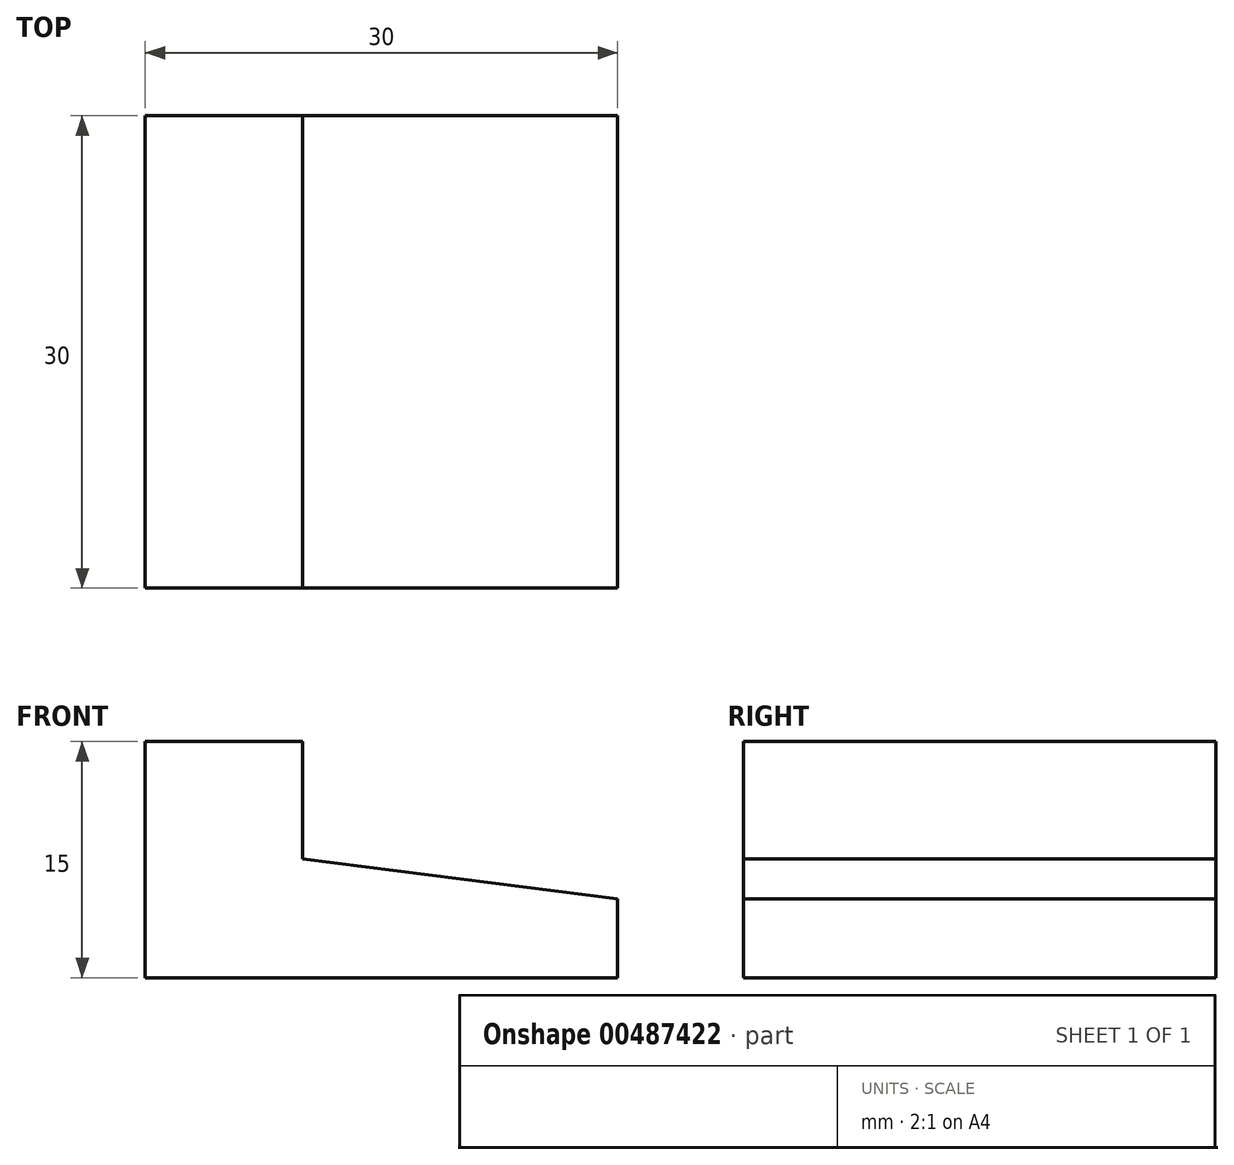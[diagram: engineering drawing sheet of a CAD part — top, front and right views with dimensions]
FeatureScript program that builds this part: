
annotation { "Feature Type Name" : "Feature", "Feature Type Description" : "" }
export const myFeature = defineFeature(function(context is Context, id is Id, definition is map)
    precondition{}
    {
        {
            var Q0;
            Q0=qCreatedBy(makeId("Top.planeOp"),FACE);
            var sketch = newSketch(context, id + "F0", { "sketchPlane" : qUnion([Q0])});
            skLineSegment(sketch, "E0.bottom", {"start": v(-27.27, 9.78) * mm, "end": v(2.73, 9.78) * mm});
            skLineSegment(sketch, "E0.top", {"start": v(-27.27, -20.22) * mm, "end": v(2.73, -20.22) * mm});
            skLineSegment(sketch, "E0.left", {"start": v(-27.27, 9.78) * mm, "end": v(-27.27, -20.22) * mm});
            skLineSegment(sketch, "E0.right", {"start": v(2.73, 9.78) * mm, "end": v(2.73, -20.22) * mm});
            skSolve(sketch);
        }
        {
            var Q0;
            Q0=makeQuery(id+"F0.imprint","IMPRINT",FACE,{"disambiguationData":[TD([[makeQuery(id+"F0.imprint","IMPRINT",EDGE,{"derivedFrom":sQuery(id+"F0.wireOp",EDGE,"E0.bottom")}),-1.0]])]});
            extrude(context, id + "F1", {"entities" : qUnion([Q0]), "depth" : 15 * mm});
        }
        {
            var Q0;
            Q0=makeQuery(id+"F1.opExtrude","SWEPT_FACE",FACE,{"disambiguationData":[OSD([sQuery(id+"F0.wireOp",EDGE,"E0.top")])]});
            var sketch = newSketch(context, id + "F2", { "sketchPlane" : qUnion([Q0])});
            skLineSegment(sketch, "E1", {"start": v(-27.27, 15) * mm, "end": v(-17.27, 15) * mm});
            skLineSegment(sketch, "E2", {"start": v(-17.27, 15) * mm, "end": v(-17.27, 7.56) * mm});
            skLineSegment(sketch, "E3", {"start": v(-17.27, 7.56) * mm, "end": v(2.73, 5) * mm});
            skSolve(sketch);
        }
        {
            var Q0;
            {var subQ0=sQuery(id+"F2.wireOp",EDGE,"E2");Q0=makeQuery(id+"F2.imprint","IMPRINT",FACE,{"disambiguationData":[TD([[makeQuery(id+"F2.imprint","IMPRINT",EDGE,{"derivedFrom":subQ0}),1.0]])]});}
            extrude(context, id + "F3", {"entities" : qUnion([Q0]), "operationType" : NewBodyOperationType.REMOVE, "endBound" : BoundingType.THROUGH_ALL, "oppositeDirection" : true, "depth" : 25.4 * mm});
        }
    });
